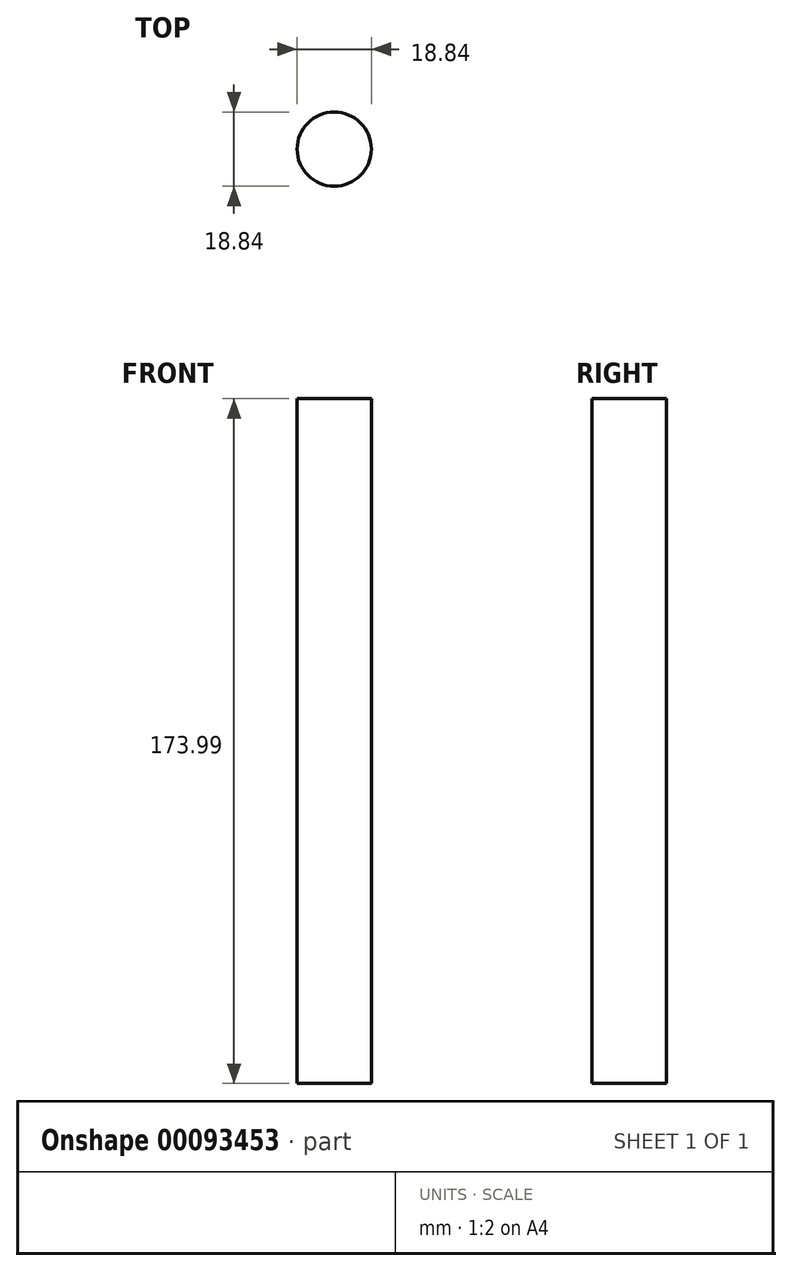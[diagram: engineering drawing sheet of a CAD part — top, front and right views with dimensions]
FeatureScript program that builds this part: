
annotation { "Feature Type Name" : "Feature", "Feature Type Description" : "" }
export const myFeature = defineFeature(function(context is Context, id is Id, definition is map)
    precondition{}
    {
        {
            var Q0;
            Q0=qCreatedBy(makeId("Top.planeOp"),FACE);
            var sketch = newSketch(context, id + "F0", { "sketchPlane" : qUnion([Q0])});
            skCircle(sketch, "E0", {"center": v(-30.48, -32.21) * mm, "radius": 9.42 * mm});
            skSolve(sketch);
        }
        {
            var Q0;
            Q0=makeQuery(id+"F0.imprint","IMPRINT",FACE,{"disambiguationData":[TD([[makeQuery(id+"F0.imprint","IMPRINT",EDGE,{"derivedFrom":sQuery(id+"F0.wireOp",EDGE,"E0")}),1.0]])]});
            extrude(context, id + "F1", {"entities" : qUnion([Q0]), "oppositeDirection" : true, "depth" : 174 * mm});
        }
    });
